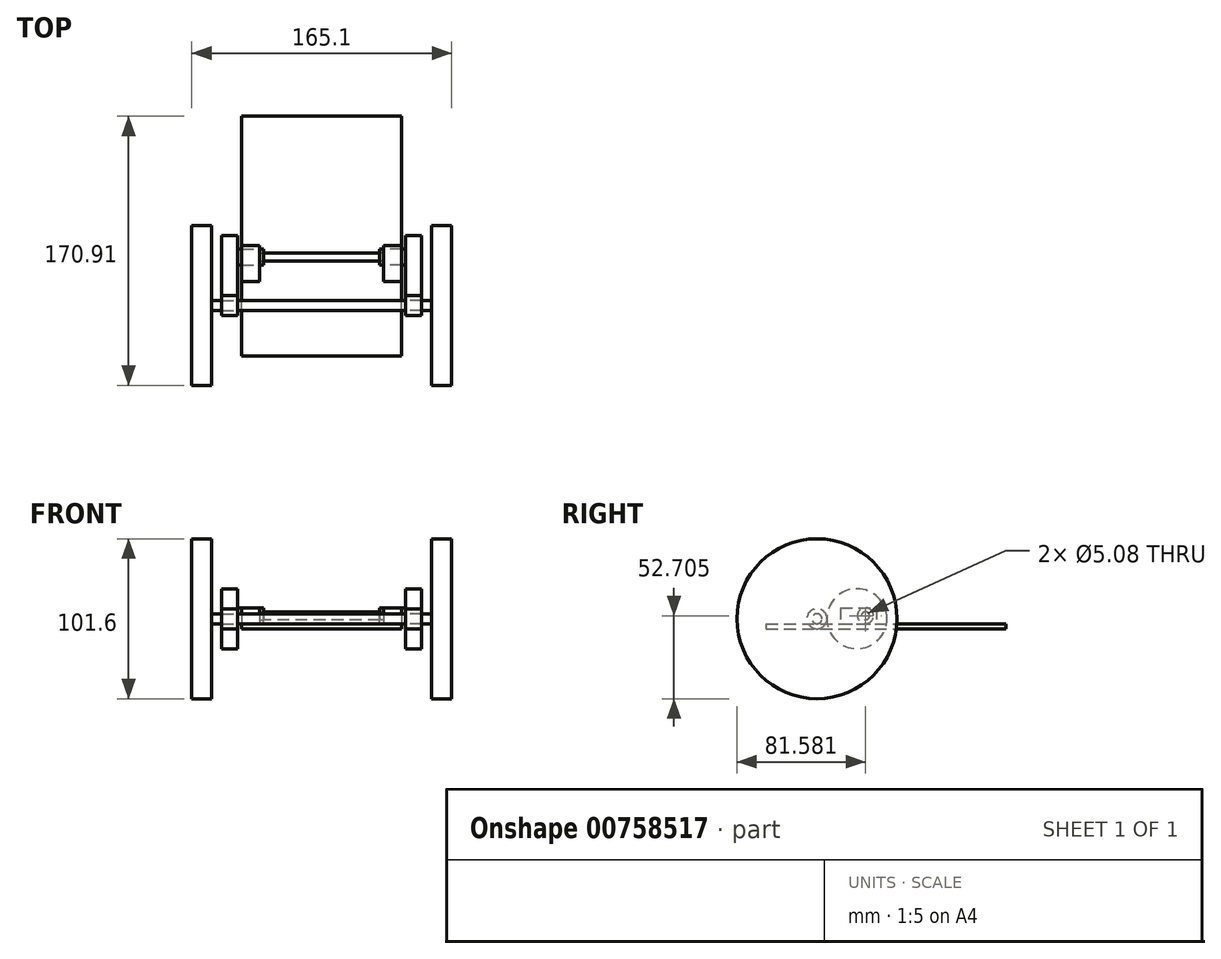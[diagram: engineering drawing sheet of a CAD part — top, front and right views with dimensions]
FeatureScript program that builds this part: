
annotation { "Feature Type Name" : "Feature", "Feature Type Description" : "" }
export const myFeature = defineFeature(function(context is Context, id is Id, definition is map)
    precondition{}
    {
        {
            var Q0;
            Q0=qCreatedBy(makeId("Top.planeOp"),FACE);
            var sketch = newSketch(context, id + "F0", { "sketchPlane" : qUnion([Q0])});
            skLineSegment(sketch, "E0.bottom", {"start": v(50.8, -76.2) * mm, "end": v(-50.8, -76.2) * mm});
            skLineSegment(sketch, "E0.top", {"start": v(50.8, 76.2) * mm, "end": v(-50.8, 76.2) * mm});
            skLineSegment(sketch, "E0.left", {"start": v(50.8, -76.2) * mm, "end": v(50.8, 76.2) * mm});
            skLineSegment(sketch, "E0.right", {"start": v(-50.8, -76.2) * mm, "end": v(-50.8, 76.2) * mm});
            skPoint(sketch, "E0.middle", {"position": v(0, 0) * mm});
            skSolve(sketch);
        }
        {
            var Q0;
            Q0 = qSketchRegion(id + "F0", true);
            extrude(context, id + "F1", {"entities" : qUnion([Q0]), "depth" : 3.17 * mm, "offsetDistance" : 25.4 * mm});
        }
        {
            var Q0;
            Q0=makeQuery(id+"F1.opExtrude","SWEPT_FACE",FACE,{"disambiguationData":[OSD([sQuery(id+"F0.wireOp",EDGE,"E0.left")])]});
            var sketch = newSketch(context, id + "F2", { "sketchPlane" : qUnion([Q0])});
            skCircle(sketch, "E1", {"center": v(-43.9, 6.35) * mm, "radius": 3.18 * mm});
            skSolve(sketch);
        }
        {
            var Q0;
            Q0=makeQuery(id+"F2.imprint","IMPRINT",FACE,{"disambiguationData":[TD([[makeQuery(id+"F2.imprint","IMPRINT",EDGE,{"derivedFrom":sQuery(id+"F2.wireOp",EDGE,"E1")}),1.0]])]});
            extrude(context, id + "F3", {"entities" : qUnion([Q0]), "oppositeDirection" : true, "depth" : 114.3 * mm, "offsetDistance" : 25.4 * mm});
        }
        {
            var Q0;
            Q0=makeQuery(id+"F3.opExtrude","CAP_FACE",FACE,{"disambiguationData":[OSD([sQuery(id+"F2.wireOp",EDGE,"E1")])],"isStart":true});
            extrude(context, id + "F4", {"entities" : qUnion([Q0]), "operationType" : NewBodyOperationType.ADD, "depth" : 12.7 * mm, "offsetDistance" : 25.4 * mm});
        }
        {
            var Q0;
            Q0=makeQuery(id+"F4.opExtrude","CAP_FACE",FACE,{"disambiguationData":[OSD([sQuery(id+"F2.wireOp",EDGE,"E1")])],"isStart":false});
            var sketch = newSketch(context, id + "F5", { "sketchPlane" : qUnion([Q0])});
            skCircle(sketch, "E2", {"center": v(-43.9, 6.35) * mm, "radius": 6.35 * mm});
            skSolve(sketch);
        }
        {
            var Q0;
            Q0=makeQuery(id+"F5.imprint","IMPRINT",FACE,{"disambiguationData":[TD([[makeQuery(id+"F5.imprint","IMPRINT",EDGE,{"derivedFrom":sQuery(id+"F5.wireOp",EDGE,"E2")}),1.0]])]});
            extrude(context, id + "F6", {"entities" : qUnion([Q0]), "operationType" : NewBodyOperationType.ADD, "oppositeDirection" : true, "depth" : 10.16 * mm, "offsetDistance" : 25.4 * mm});
        }
        {
            var Q0;
            {var subQ0=sQuery(id+"F2.wireOp",EDGE,"E1");Q0=makeQuery(id+"F6.boolean.opBoolean","MERGE",FACE,{"derivedFrom":[makeQuery(id+"F4.opExtrude","CAP_FACE",FACE,{"disambiguationData":[OSD([subQ0])],"isStart":false}),makeQuery(id+"F6.opExtrude","CAP_FACE",FACE,{"disambiguationData":[OSD([subQ0,sQuery(id+"F5.wireOp",EDGE,"E2")])],"isStart":true})]});}
            var sketch = newSketch(context, id + "F7", { "sketchPlane" : qUnion([Q0])});
            skCircle(sketch, "E3", {"center": v(-43.9, 6.35) * mm, "radius": 3.18 * mm});
            skSolve(sketch);
        }
        {
            var Q0;
            Q0 = qSketchRegion(id + "F7", true);
            extrude(context, id + "F8", {"entities" : qUnion([Q0]), "operationType" : NewBodyOperationType.ADD, "depth" : 6.35 * mm, "offsetDistance" : 25.4 * mm});
        }
        {
            var Q0;
            Q0=makeQuery(id+"F8.opExtrude","CAP_FACE",FACE,{"disambiguationData":[OSD([sQuery(id+"F7.wireOp",EDGE,"E3")])],"isStart":false});
            var sketch = newSketch(context, id + "F9", { "sketchPlane" : qUnion([Q0])});
            skLineSegment(sketch, "E4", {"start": v(-43.9, 6.35) * mm, "end": v(-18.5, 6.35) * mm});
            skCircle(sketch, "E5", {"center": v(-18.5, 6.35) * mm, "radius": 19.05 * mm});
            skSolve(sketch);
        }
        {
            var Q0;
            Q0=makeQuery(id+"F9.imprint","IMPRINT",FACE,{"disambiguationData":[TD([[makeQuery(id+"F9.imprint","IMPRINT",EDGE,{"derivedFrom":sQuery(id+"F9.wireOp",EDGE,"E5")}),1.0]])]});
            extrude(context, id + "F10", {"entities" : qUnion([Q0]), "oppositeDirection" : true, "depth" : 16.5 * mm, "offsetDistance" : 25.4 * mm});
        }
        {
            var Q0;
            Q0=makeQuery(id+"F1.opExtrude","CAP_FACE",FACE,{"disambiguationData":[OSD([sQuery(id+"F0.wireOp",EDGE,"E0.bottom"),sQuery(id+"F0.wireOp",EDGE,"E0.top"),sQuery(id+"F0.wireOp",EDGE,"E0.left"),sQuery(id+"F0.wireOp",EDGE,"E0.right")])],"isStart":false});
            var sketch = newSketch(context, id + "F11", { "sketchPlane" : qUnion([Q0])});
            skLineSegment(sketch, "E6.bottom", {"start": v(50.8, -6.1) * mm, "end": v(39.37, -6.1) * mm});
            skLineSegment(sketch, "E6.top", {"start": v(50.8, -28.95) * mm, "end": v(39.37, -28.95) * mm});
            skLineSegment(sketch, "E6.left", {"start": v(50.8, -6.1) * mm, "end": v(50.8, -28.95) * mm});
            skLineSegment(sketch, "E6.right", {"start": v(39.37, -6.1) * mm, "end": v(39.37, -28.95) * mm});
            skPoint(sketch, "E7", {"position": v(39.37, -28.95) * mm});
            skSolve(sketch);
        }
        {
            var Q0;
            Q0=makeQuery(id+"F11.imprint","IMPRINT",FACE,{"disambiguationData":[TD([[makeQuery(id+"F11.imprint","IMPRINT",EDGE,{"derivedFrom":sQuery(id+"F11.wireOp",EDGE,"E6.bottom")}),1.0]])]});
            extrude(context, id + "F12", {"entities" : qUnion([Q0]), "depth" : 10.16 * mm, "offsetDistance" : 25.4 * mm});
        }
        {
            var Q0;
            Q0=makeQuery(id+"F12.opExtrude","SWEPT_FACE",FACE,{"disambiguationData":[OSD([sQuery(id+"F11.wireOp",EDGE,"E6.right")])]});
            var sketch = newSketch(context, id + "F13", { "sketchPlane" : qUnion([Q0])});
            skCircle(sketch, "E8", {"center": v(13.13, 8.26) * mm, "radius": 5.08 * mm});
            skSolve(sketch);
        }
        {
            var Q0;
            {var subQ0=sQuery(id+"F13.wireOp",EDGE,"E8");var subQ1=sQuery(id+"F11.wireOp",EDGE,"E6.right");var subQ2=makeQuery(id+"F13.imprint","INTERSECT",VERTEX,{"derivedFrom":[makeQuery(id+"F12.opExtrude","CAP_EDGE",EDGE,{"disambiguationData":[OSD([subQ1])],"isStart":true}),subQ0]});Q0=makeQuery(id+"F13.imprint","IMPRINT",FACE,{"disambiguationData":[TD([[makeQuery(id+"F13.imprint","IMPRINT",EDGE,{"disambiguationData":[TD([[subQ2,1.0]])],"derivedFrom":subQ0}),1.0]])]});}
            extrude(context, id + "F14", {"entities" : qUnion([Q0]), "depth" : 2.54 * mm, "offsetDistance" : 25.4 * mm});
        }
        {
            var Q0;
            Q0=makeQuery(id+"F14.opExtrude","CAP_FACE",FACE,{"disambiguationData":[OSD([sQuery(id+"F13.wireOp",EDGE,"E8")])],"isStart":false});
            var sketch = newSketch(context, id + "F15", { "sketchPlane" : qUnion([Q0])});
            skCircle(sketch, "E9", {"center": v(13.13, 8.26) * mm, "radius": 2.54 * mm});
            skSolve(sketch);
        }
        {
            var Q0;
            Q0=makeQuery(id+"F15.imprint","IMPRINT",FACE,{"disambiguationData":[TD([[makeQuery(id+"F15.imprint","IMPRINT",EDGE,{"derivedFrom":sQuery(id+"F15.wireOp",EDGE,"E9")}),1.0]])]});
            extrude(context, id + "F16", {"entities" : qUnion([Q0]), "depth" : 73.66 * mm, "offsetDistance" : 25.4 * mm});
        }
        {
            var Q0;
            Q0=makeQuery(id+"F10.opExtrude","CAP_FACE",FACE,{"disambiguationData":[OSD([sQuery(id+"F9.wireOp",EDGE,"E5")])],"isStart":true});
            extrude(context, id + "F17", {"entities" : qUnion([Q0]), "operationType" : NewBodyOperationType.REMOVE, "oppositeDirection" : true, "depth" : 3.8 * mm, "offsetDistance" : 25.4 * mm});
        }
        {
            var Q0;
            Q0=makeQuery(id+"F16.opExtrude","CAP_FACE",FACE,{"disambiguationData":[OSD([sQuery(id+"F15.wireOp",EDGE,"E9")])],"isStart":false});
            var sketch = newSketch(context, id + "F18", { "sketchPlane" : qUnion([Q0])});
            skCircle(sketch, "E10", {"center": v(13.13, 8.26) * mm, "radius": 5.08 * mm});
            skSolve(sketch);
        }
        {
            var Q0;
            Q0=makeQuery(id+"F18.imprint","IMPRINT",FACE,{"disambiguationData":[TD([[makeQuery(id+"F18.imprint","IMPRINT",EDGE,{"derivedFrom":sQuery(id+"F18.wireOp",EDGE,"E10")}),1.0]])]});
            extrude(context, id + "F19", {"entities" : qUnion([Q0]), "depth" : 2.54 * mm, "offsetDistance" : 25.4 * mm});
        }
        {
            var Q0;
            Q0=makeQuery(id+"F14.opExtrude","CAP_FACE",FACE,{"disambiguationData":[OSD([sQuery(id+"F13.wireOp",EDGE,"E8")])],"isStart":false});
            extrude(context, id + "F20", {"entities" : qUnion([Q0]), "oppositeDirection" : true, "depth" : 16.5 * mm, "offsetDistance" : 25.4 * mm});
        }
        {
            var Q0;
            Q0=makeQuery(id+"F17.boolean.opBoolean","COPY",FACE,{"derivedFrom":makeQuery(id+"F17.opExtrude","CAP_FACE",FACE,{"disambiguationData":[OSD([sQuery(id+"F9.wireOp",EDGE,"E5")])],"isStart":false})});
            extrude(context, id + "F21", {"entities" : qUnion([Q0]), "operationType" : NewBodyOperationType.REMOVE, "oppositeDirection" : true, "depth" : 2.54 * mm, "offsetDistance" : 25.4 * mm});
        }
        {
            var Q0;
            Q0=makeQuery(id+"F8.opExtrude","CAP_FACE",FACE,{"disambiguationData":[OSD([sQuery(id+"F7.wireOp",EDGE,"E3")])],"isStart":false});
            var sketch = newSketch(context, id + "F22", { "sketchPlane" : qUnion([Q0])});
            skCircle(sketch, "E11", {"center": v(-43.9, 6.35) * mm, "radius": 50.8 * mm});
            skSolve(sketch);
        }
        {
            var Q0;
            Q0 = qSketchRegion(id + "F22", true);
            extrude(context, id + "F23", {"entities" : qUnion([Q0]), "operationType" : NewBodyOperationType.ADD, "depth" : 12.7 * mm, "offsetDistance" : 25.4 * mm});
        }
        {
            var Q0;
            Q0=makeQuery(id+"F1.opExtrude","CAP_FACE",FACE,{"disambiguationData":[OSD([sQuery(id+"F0.wireOp",EDGE,"E0.bottom"),sQuery(id+"F0.wireOp",EDGE,"E0.top"),sQuery(id+"F0.wireOp",EDGE,"E0.left"),sQuery(id+"F0.wireOp",EDGE,"E0.right")])],"isStart":false});
            var sketch = newSketch(context, id + "F24", { "sketchPlane" : qUnion([Q0])});
            skSolve(sketch);
        }
        {
            var Q0;
            Q0=makeQuery(id+"F16.opExtrude","CAP_FACE",FACE,{"disambiguationData":[OSD([sQuery(id+"F15.wireOp",EDGE,"E9")])],"isStart":false});
            extrude(context, id + "F25", {"entities" : qUnion([Q0]), "depth" : 2.54 * mm, "offsetDistance" : 25.4 * mm});
        }
        {
            var Q0;
            Q0=makeQuery(id+"F1.opExtrude","CAP_EDGE",EDGE,{"disambiguationData":[OSD([sQuery(id+"F0.wireOp",EDGE,"E0.top")])],"isStart":false});
            cPoint(context, id + "F26", {"entities" : qUnion([Q0]), "parameter" : 0.5});
        }
        {
            var Q0;
            Q0=makeQuery(id+"F1.opExtrude","CAP_EDGE",EDGE,{"disambiguationData":[OSD([sQuery(id+"F0.wireOp",EDGE,"E0.bottom")])],"isStart":false});
            cPoint(context, id + "F27", {"entities" : qUnion([Q0]), "parameter" : 0.5});
        }
        {
            var Q0;
            Q0 = qCreatedBy(id + "F26" ,VERTEX);
            var Q1;
            Q1=sQuery(id+"F0.wireOp",VERTEX,"E0.middle");
            var Q2;
            Q2 = qCreatedBy(id + "F27" ,VERTEX);
            cPlane(context, id + "F28", {"entities" : qUnion([Q0, Q1, Q2]), "cplaneType" : CPlaneType.THREE_POINT, "offset" : 25.4 * mm, "width" : 152.4 * mm, "height" : 152.4 * mm});
        }
        {
            var Q0;
            Q0=makeQuery(id+"F3.opExtrude","SWEPT_BODY",BODY,{"disambiguationData":[OSD([sQuery(id+"F2.wireOp",EDGE,"E1")])]});
            var Q1;
            Q1=makeQuery(id+"F10.opExtrude","SWEPT_BODY",BODY,{"disambiguationData":[OSD([sQuery(id+"F9.wireOp",EDGE,"E5")])]});
            var Q2;
            Q2=makeQuery(id+"F12.opExtrude","SWEPT_BODY",BODY,{"disambiguationData":[OSD([sQuery(id+"F11.wireOp",EDGE,"E6.bottom"),sQuery(id+"F11.wireOp",EDGE,"E6.top"),sQuery(id+"F11.wireOp",EDGE,"E6.left"),sQuery(id+"F11.wireOp",EDGE,"E6.right")])]});
            var Q3;
            Q3=makeQuery(id+"F14.opExtrude","SWEPT_BODY",BODY,{"disambiguationData":[OSD([sQuery(id+"F13.wireOp",EDGE,"E8")])]});
            var Q4;
            Q4=makeQuery(id+"F16.opExtrude","SWEPT_BODY",BODY,{"disambiguationData":[OSD([sQuery(id+"F15.wireOp",EDGE,"E9")])]});
            var Q5;
            Q5=makeQuery(id+"F20.opExtrude","SWEPT_BODY",BODY,{"disambiguationData":[OSD([sQuery(id+"F13.wireOp",EDGE,"E8")])]});
            var Q6;
            Q6=makeQuery(id+"F19.opExtrude","SWEPT_BODY",BODY,{"disambiguationData":[OSD([sQuery(id+"F15.wireOp",EDGE,"E9"),sQuery(id+"F18.wireOp",EDGE,"E10")])]});
            var Q7;
            Q7=qCreatedBy(id+"F28.planeOp",FACE);
            mirror(context, id + "F29", {"entities" : qUnion([Q0, Q1, Q2, Q3, Q4, Q5, Q6]), "mirrorPlane" : qUnion([Q7])});
        }
    });
